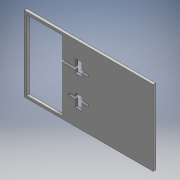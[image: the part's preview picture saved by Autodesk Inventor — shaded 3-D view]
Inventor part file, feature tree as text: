
AUTODESK INVENTOR PART (.ipt)
format: ipt  version: 2016 (Build 200138000, 138)  size: 141,824 bytes
history: native  units: mm
features: extrude x1, sketch x1
ambient origin geometry x8: Origin, YZ Plane, XZ Plane, XY Plane, X Axis, Y Axis, Z Axis, Center Point
bodies: Body1 (feature_tree)
feature tree (2):
  extrude  "Extrusion4"  Depth=59.0mm
  sketch  "Sketch1"  dims[d0=101.0mm d1=59.0mm d4=5.0mm d5=10.0mm d6=10.0mm d7=2.0mm d8=5.0mm d14=20.0mm d15=2.0mm d16=2.0mm d17=55.0mm d18=2.0mm d19=28.0mm d25=2.0mm d26=0.0mm d27=42.5mm]
